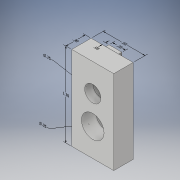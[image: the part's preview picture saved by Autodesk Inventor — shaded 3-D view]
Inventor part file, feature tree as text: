
AUTODESK INVENTOR PART (.ipt)
format: ipt  version: 2018 (Build 220112000, 112)  size: 158,720 bytes
history: native  units: in
note: dims shown in document units (in); Inventor stores cm internally (conversion verified against a paired STEP export)
features: other x10, sketch x3, hole x2, extrude x1
ambient origin geometry x8: Origin, YZ Plane, XZ Plane, XY Plane, X Axis, Y Axis, Z Axis, Center Point
bodies: Solid1 (feature_tree)
feature tree (16):
  other  "Annotations"
  extrude  "Extrusion1"  Depth=0.3in
  hole  "Hole1"  [1 undecoded]
  hole  "Hole4"  [1 undecoded]
  sketch  "Sketch1"  dims[d0=0.65in d1=0.3in]
  sketch  "Sketch4"  dims[d2=0.2in d3=0.05in]
  sketch  "Sketch6"  dims[d4=1.3in d5=0.0in d8=0.43in d9=0.43in d10=0.12in d11=0.75in d12=0.25in d13=0.13in d14=0.5635in d15=1.0in d16=0.8108in d31=0.2in d32=0.75in d33=0.35in d34=0.22in d35=0.5635in d36=1.0in d37=0.8108in d38=0.0665in d39=0.3373in d40=0.3in d41=0.0661in d42=0.1569in d43=1.3in d44=0.2119in d45=0.2631in d46=0.65in d47=0.1693in d48=0.187in d49=0.2in d50=0.2107in d51=0.2526in d52=0.0508in d53=0.1096in d54=0.078in d55=-0.1799in d56=0.25in d57=2.2945in d58=0.1687in d59=-0.1394in d60=0.35in d61=0.1056in d62=0.1774in d63=0.0762in d64=0.12in d65=2.4113in d66=0.2972in d67=0.0636in d68=0.2in]
  other  "Linear Dimension 1"
  other  "Linear Dimension 2"
  other  "Linear Dimension 3"
  other  "Linear Dimension 4"
  other  "Linear Dimension 5"
  other  "Diameter Dimension 1"
  other  "Diameter Dimension 2"
  other  "Diameter Dimension 3"
  other  "Diameter Dimension 4"
note: 2 required parameter values undecoded (feature->parameter linkage not recoverable at this tier; creation-order binding heuristic only, values carry confidence <= 0.55)
